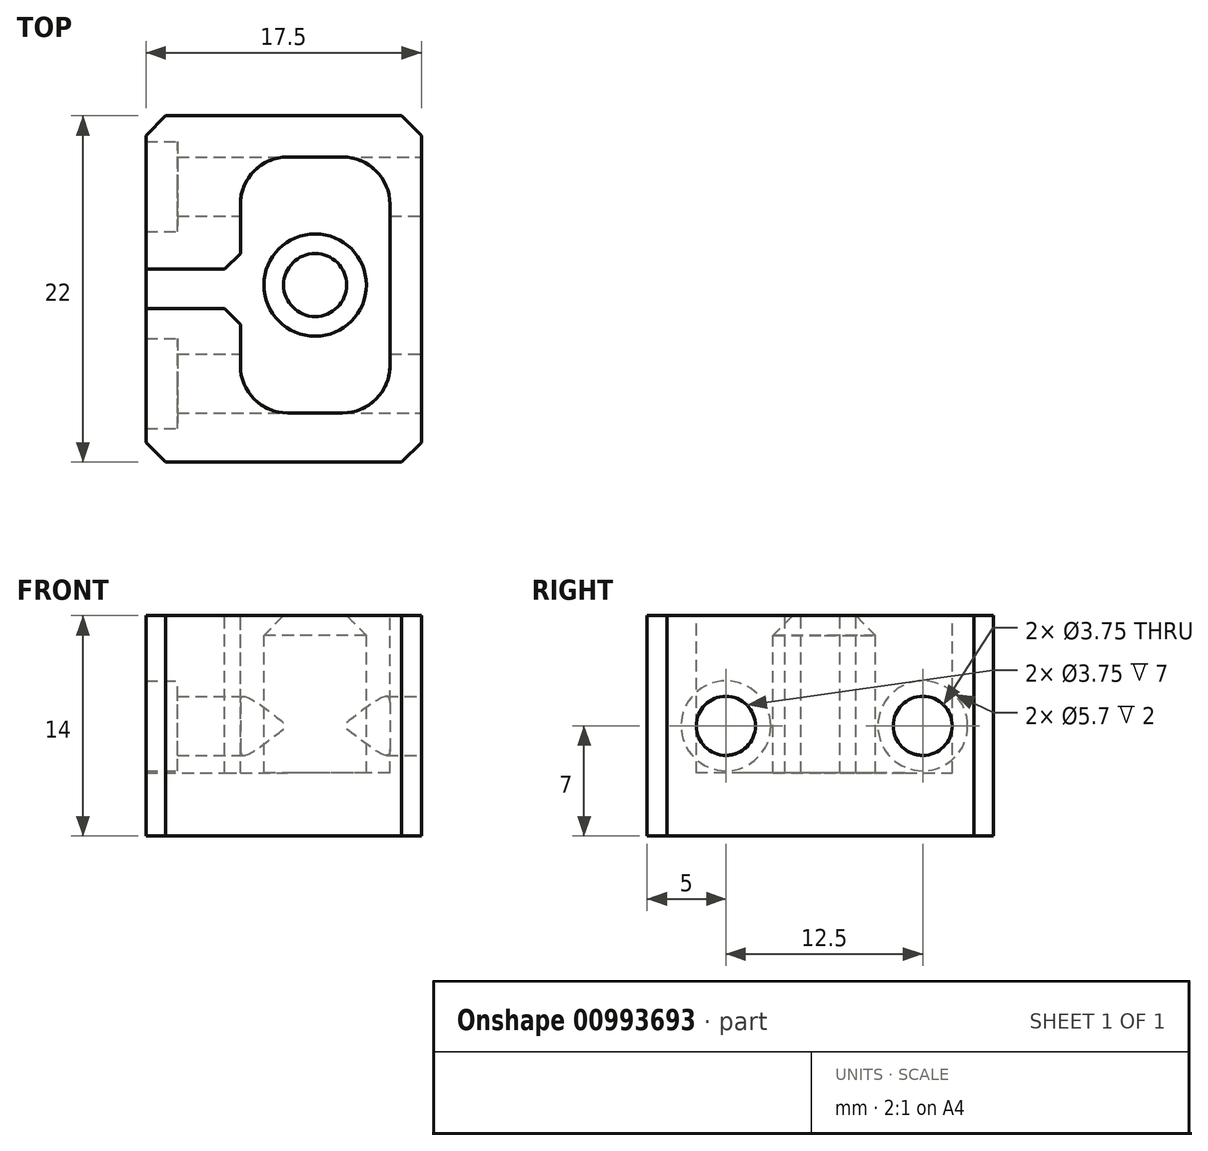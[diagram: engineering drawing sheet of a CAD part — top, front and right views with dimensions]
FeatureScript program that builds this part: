
annotation { "Feature Type Name" : "Feature", "Feature Type Description" : "" }
export const myFeature = defineFeature(function(context is Context, id is Id, definition is map)
    precondition{}
    {
        {
            var Q0;
            Q0=qCreatedBy(makeId("Top.planeOp"),FACE);
            var sketch = newSketch(context, id + "F0", { "sketchPlane" : qUnion([Q0])});
            skLineSegment(sketch, "E0.bottom", {"start": v(8.75, 11) * mm, "end": v(-8.75, 11) * mm});
            skLineSegment(sketch, "E0.top", {"start": v(8.75, -11) * mm, "end": v(-8.75, -11) * mm});
            skLineSegment(sketch, "E0.left", {"start": v(8.75, 11) * mm, "end": v(8.75, -11) * mm});
            skLineSegment(sketch, "E0.right", {"start": v(-8.75, 11) * mm, "end": v(-8.75, -11) * mm});
            skPoint(sketch, "E0.middle", {"position": v(0, 0) * mm});
            skLineSegment(sketch, "E1", {"start": v(-6.75, 8.37) * mm, "end": v(8.75, 8.38) * mm});
            skLineSegment(sketch, "E2", {"start": v(8.75, 4.63) * mm, "end": v(-6.75, 4.62) * mm});
            skLineSegment(sketch, "E3", {"start": v(8.75, -4.12) * mm, "end": v(-6.75, -4.13) * mm});
            skLineSegment(sketch, "E4", {"start": v(8.75, -7.87) * mm, "end": v(-6.75, -7.88) * mm});
            skLineSegment(sketch, "E5", {"start": v(-8.75, -1.25) * mm, "end": v(-2.75, -1.25) * mm});
            skLineSegment(sketch, "E6", {"start": v(-8.75, 1.25) * mm, "end": v(-2.75, 1.25) * mm});
            skLineSegment(sketch, "E7", {"start": v(-2.75, 1.25) * mm, "end": v(-2.75, 11) * mm});
            skLineSegment(sketch, "E8", {"start": v(-2.75, -1.25) * mm, "end": v(-2.75, -11) * mm});
            skCircle(sketch, "E9", {"center": v(2, 0.25) * mm, "radius": 4.75 * mm, "construction": true});
            skCircle(sketch, "E10", {"center": v(2, 0.25) * mm, "radius": 3.25 * mm});
            skLineSegment(sketch, "E11", {"start": v(-3.75, 1.25) * mm, "end": v(-2.75, 2.25) * mm});
            skLineSegment(sketch, "E12", {"start": v(-3.75, -1.25) * mm, "end": v(-2.75, -2.25) * mm});
            skLineSegment(sketch, "E13", {"start": v(6.75, 11) * mm, "end": v(6.75, -11) * mm});
            skLineSegment(sketch, "E14", {"start": v(-8.75, 6.5) * mm, "end": v(8.75, 6.5) * mm});
            skLineSegment(sketch, "E15", {"start": v(-8.75, -6) * mm, "end": v(8.75, -6) * mm});
            skLineSegment(sketch, "E16", {"start": v(-6.75, 8.37) * mm, "end": v(-6.75, 9.35) * mm});
            skLineSegment(sketch, "E17", {"start": v(-6.75, 9.35) * mm, "end": v(-8.75, 9.35) * mm});
            skLineSegment(sketch, "E18", {"start": v(-6.75, 4.62) * mm, "end": v(-6.75, 3.65) * mm});
            skLineSegment(sketch, "E19", {"start": v(-6.75, 3.65) * mm, "end": v(-8.75, 3.65) * mm});
            skLineSegment(sketch, "E20", {"start": v(-6.75, -4.13) * mm, "end": v(-6.75, -3.15) * mm});
            skLineSegment(sketch, "E21", {"start": v(-6.75, -3.15) * mm, "end": v(-8.75, -3.15) * mm});
            skLineSegment(sketch, "E22", {"start": v(-6.75, -7.88) * mm, "end": v(-6.75, -8.85) * mm});
            skLineSegment(sketch, "E23", {"start": v(-6.75, -8.85) * mm, "end": v(-8.75, -8.85) * mm});
            skSolve(sketch);
        }
        {
            var Q0;
            {var subQ3=sQuery(id+"F0.wireOp",EDGE,"E12");Q0=makeQuery(id+"F0.imprint","IMPRINT",FACE,{"disambiguationData":[TD([[makeQuery(id+"F0.imprint","IMPRINT",EDGE,{"derivedFrom":subQ3}),-1.0]])]});}
            var Q1;
            {var subQ0=sQuery(id+"F0.wireOp",EDGE,"E1");var subQ1=sQuery(id+"F0.wireOp",EDGE,"E0.right");var subQ2=makeQuery(id+"F0.imprint","INTERSECT",VERTEX,{"derivedFrom":[subQ1,subQ0]});Q1=makeQuery(id+"F0.imprint","IMPRINT",FACE,{"disambiguationData":[TD([[makeQuery(id+"F0.imprint","IMPRINT",EDGE,{"disambiguationData":[TD([[subQ2,-1.0]])],"derivedFrom":subQ1}),1.0]])]});}
            var Q2;
            {var subQ0=sQuery(id+"F0.wireOp",EDGE,"E1");var subQ1=sQuery(id+"F0.wireOp",EDGE,"E0.left");var subQ2=makeQuery(id+"F0.imprint","INTERSECT",VERTEX,{"derivedFrom":[subQ1,subQ0]});Q2=makeQuery(id+"F0.imprint","IMPRINT",FACE,{"disambiguationData":[TD([[makeQuery(id+"F0.imprint","IMPRINT",EDGE,{"disambiguationData":[TD([[subQ2,-1.0]])],"derivedFrom":subQ1}),-1.0]])]});}
            var Q3;
            {var subQ0=sQuery(id+"F0.wireOp",EDGE,"E3");var subQ1=sQuery(id+"F0.wireOp",EDGE,"E0.left");var subQ2=makeQuery(id+"F0.imprint","INTERSECT",VERTEX,{"derivedFrom":[subQ1,subQ0]});Q3=makeQuery(id+"F0.imprint","IMPRINT",FACE,{"disambiguationData":[TD([[makeQuery(id+"F0.imprint","IMPRINT",EDGE,{"disambiguationData":[TD([[subQ2,-1.0]])],"derivedFrom":subQ1}),-1.0]])]});}
            var Q4;
            {var subQ0=sQuery(id+"F0.wireOp",EDGE,"E0.right");var subQ1=sQuery(id+"F0.wireOp",EDGE,"E0.bottom");var subQ2=makeQuery(id+"F0.imprint","INTERSECT",VERTEX,{"derivedFrom":[subQ1,subQ0]});Q4=makeQuery(id+"F0.imprint","IMPRINT",FACE,{"disambiguationData":[TD([[makeQuery(id+"F0.imprint","IMPRINT",EDGE,{"disambiguationData":[TD([[subQ2,1.0]])],"derivedFrom":subQ1}),1.0]])]});}
            var Q5;
            {var subQ0=sQuery(id+"F0.wireOp",EDGE,"E0.left");var subQ1=sQuery(id+"F0.wireOp",EDGE,"E0.top");var subQ2=makeQuery(id+"F0.imprint","INTERSECT",VERTEX,{"derivedFrom":[subQ1,subQ0]});Q5=makeQuery(id+"F0.imprint","IMPRINT",FACE,{"disambiguationData":[TD([[makeQuery(id+"F0.imprint","IMPRINT",EDGE,{"disambiguationData":[TD([[subQ2,-1.0]])],"derivedFrom":subQ1}),-1.0]])]});}
            var Q6;
            {var subQ0=sQuery(id+"F0.wireOp",EDGE,"E3");var subQ1=sQuery(id+"F0.wireOp",EDGE,"E0.right");var subQ2=makeQuery(id+"F0.imprint","INTERSECT",VERTEX,{"derivedFrom":[subQ1,subQ0]});Q6=makeQuery(id+"F0.imprint","IMPRINT",FACE,{"disambiguationData":[TD([[makeQuery(id+"F0.imprint","IMPRINT",EDGE,{"disambiguationData":[TD([[subQ2,-1.0]])],"derivedFrom":subQ1}),1.0]])]});}
            var Q7;
            {var subQ0=sQuery(id+"F0.wireOp",EDGE,"E0.right");var subQ1=sQuery(id+"F0.wireOp",EDGE,"E0.top");var subQ2=makeQuery(id+"F0.imprint","INTERSECT",VERTEX,{"derivedFrom":[subQ1,subQ0]});Q7=makeQuery(id+"F0.imprint","IMPRINT",FACE,{"disambiguationData":[TD([[makeQuery(id+"F0.imprint","IMPRINT",EDGE,{"disambiguationData":[TD([[subQ2,1.0]])],"derivedFrom":subQ1}),-1.0]])]});}
            var Q8;
            {var subQ0=sQuery(id+"F0.wireOp",EDGE,"E0.left");var subQ1=sQuery(id+"F0.wireOp",EDGE,"E0.bottom");var subQ2=makeQuery(id+"F0.imprint","INTERSECT",VERTEX,{"derivedFrom":[subQ1,subQ0]});Q8=makeQuery(id+"F0.imprint","IMPRINT",FACE,{"disambiguationData":[TD([[makeQuery(id+"F0.imprint","IMPRINT",EDGE,{"disambiguationData":[TD([[subQ2,-1.0]])],"derivedFrom":subQ1}),1.0]])]});}
            var Q9;
            {var subQ3=sQuery(id+"F0.wireOp",EDGE,"E12");Q9=makeQuery(id+"F0.imprint","IMPRINT",FACE,{"disambiguationData":[TD([[makeQuery(id+"F0.imprint","IMPRINT",EDGE,{"derivedFrom":subQ3}),1.0]])]});}
            var Q10;
            {var subQ3=sQuery(id+"F0.wireOp",EDGE,"E11");Q10=makeQuery(id+"F0.imprint","IMPRINT",FACE,{"disambiguationData":[TD([[makeQuery(id+"F0.imprint","IMPRINT",EDGE,{"derivedFrom":subQ3}),-1.0]])]});}
            var Q11;
            {var subQ0=sQuery(id+"F0.wireOp",EDGE,"E11");Q11=makeQuery(id+"F0.imprint","IMPRINT",FACE,{"disambiguationData":[TD([[makeQuery(id+"F0.imprint","IMPRINT",EDGE,{"derivedFrom":subQ0}),1.0]])]});}
            var Q12;
            Q12=makeQuery(id+"F0.imprint","IMPRINT",FACE,{"disambiguationData":[TD([[makeQuery(id+"F0.imprint","IMPRINT",EDGE,{"derivedFrom":sQuery(id+"F0.wireOp",EDGE,"E10")}),-1.0]])]});
            var Q13;
            Q13=makeQuery(id+"F0.imprint","IMPRINT",FACE,{"disambiguationData":[TD([[makeQuery(id+"F0.imprint","IMPRINT",EDGE,{"derivedFrom":sQuery(id+"F0.wireOp",EDGE,"E10")}),1.0]])]});
            var Q14;
            {var subQ0=sQuery(id+"F0.wireOp",EDGE,"E7");var subQ1=sQuery(id+"F0.wireOp",EDGE,"E0.bottom");var subQ2=makeQuery(id+"F0.imprint","INTERSECT",VERTEX,{"derivedFrom":[subQ1,subQ0]});Q14=makeQuery(id+"F0.imprint","IMPRINT",FACE,{"disambiguationData":[TD([[makeQuery(id+"F0.imprint","IMPRINT",EDGE,{"disambiguationData":[TD([[subQ2,1.0]])],"derivedFrom":subQ1}),1.0]])]});}
            var Q15;
            {var subQ0=sQuery(id+"F0.wireOp",EDGE,"E7");var subQ1=sQuery(id+"F0.wireOp",EDGE,"E1");var subQ2=makeQuery(id+"F0.imprint","INTERSECT",VERTEX,{"derivedFrom":[subQ1,subQ0]});Q15=makeQuery(id+"F0.imprint","IMPRINT",FACE,{"disambiguationData":[TD([[makeQuery(id+"F0.imprint","IMPRINT",EDGE,{"disambiguationData":[TD([[subQ2,-1.0]])],"derivedFrom":subQ1}),-1.0]])]});}
            var Q16;
            {var subQ0=sQuery(id+"F0.wireOp",EDGE,"E2");var subQ1=sQuery(id+"F0.wireOp",EDGE,"E0.left");var subQ2=makeQuery(id+"F0.imprint","INTERSECT",VERTEX,{"derivedFrom":[subQ1,subQ0]});Q16=makeQuery(id+"F0.imprint","IMPRINT",FACE,{"disambiguationData":[TD([[makeQuery(id+"F0.imprint","IMPRINT",EDGE,{"disambiguationData":[TD([[subQ2,-1.0]])],"derivedFrom":subQ1}),-1.0]])]});}
            var Q17;
            {var subQ0=sQuery(id+"F0.wireOp",EDGE,"E13");var subQ1=sQuery(id+"F0.wireOp",EDGE,"E3");var subQ2=makeQuery(id+"F0.imprint","INTERSECT",VERTEX,{"derivedFrom":[subQ1,subQ0]});Q17=makeQuery(id+"F0.imprint","IMPRINT",FACE,{"disambiguationData":[TD([[makeQuery(id+"F0.imprint","IMPRINT",EDGE,{"disambiguationData":[TD([[subQ2,-1.0]])],"derivedFrom":subQ1}),1.0]])]});}
            var Q18;
            {var subQ0=sQuery(id+"F0.wireOp",EDGE,"E8");var subQ1=sQuery(id+"F0.wireOp",EDGE,"E0.top");var subQ2=makeQuery(id+"F0.imprint","INTERSECT",VERTEX,{"derivedFrom":[subQ1,subQ0]});Q18=makeQuery(id+"F0.imprint","IMPRINT",FACE,{"disambiguationData":[TD([[makeQuery(id+"F0.imprint","IMPRINT",EDGE,{"disambiguationData":[TD([[subQ2,1.0]])],"derivedFrom":subQ1}),-1.0]])]});}
            var Q19;
            {var subQ9=sQuery(id+"F0.wireOp",EDGE,"E16");Q19=makeQuery(id+"F0.imprint","IMPRINT",FACE,{"disambiguationData":[TD([[makeQuery(id+"F0.imprint","IMPRINT",EDGE,{"derivedFrom":subQ9}),1.0]])]});}
            var Q20;
            {var subQ6=sQuery(id+"F0.wireOp",EDGE,"E20");Q20=makeQuery(id+"F0.imprint","IMPRINT",FACE,{"disambiguationData":[TD([[makeQuery(id+"F0.imprint","IMPRINT",EDGE,{"derivedFrom":subQ6}),1.0]])]});}
            var Q21;
            {var subQ0=sQuery(id+"F0.wireOp",EDGE,"E13");var subQ1=sQuery(id+"F0.wireOp",EDGE,"E2");var subQ2=makeQuery(id+"F0.imprint","INTERSECT",VERTEX,{"derivedFrom":[subQ1,subQ0]});Q21=makeQuery(id+"F0.imprint","IMPRINT",FACE,{"disambiguationData":[TD([[makeQuery(id+"F0.imprint","IMPRINT",EDGE,{"disambiguationData":[TD([[subQ2,-1.0]])],"derivedFrom":subQ1}),-1.0]])]});}
            var Q22;
            {var subQ0=sQuery(id+"F0.wireOp",EDGE,"E2");var subQ1=sQuery(id+"F0.wireOp",EDGE,"E0.left");var subQ2=makeQuery(id+"F0.imprint","INTERSECT",VERTEX,{"derivedFrom":[subQ1,subQ0]});Q22=makeQuery(id+"F0.imprint","IMPRINT",FACE,{"disambiguationData":[TD([[makeQuery(id+"F0.imprint","IMPRINT",EDGE,{"disambiguationData":[TD([[subQ2,1.0]])],"derivedFrom":subQ1}),-1.0]])]});}
            var Q23;
            {var subQ0=sQuery(id+"F0.wireOp",EDGE,"E13");var subQ1=sQuery(id+"F0.wireOp",EDGE,"E4");var subQ2=makeQuery(id+"F0.imprint","INTERSECT",VERTEX,{"derivedFrom":[subQ1,subQ0]});Q23=makeQuery(id+"F0.imprint","IMPRINT",FACE,{"disambiguationData":[TD([[makeQuery(id+"F0.imprint","IMPRINT",EDGE,{"disambiguationData":[TD([[subQ2,-1.0]])],"derivedFrom":subQ1}),-1.0]])]});}
            var Q24;
            {var subQ0=sQuery(id+"F0.wireOp",EDGE,"E4");var subQ1=sQuery(id+"F0.wireOp",EDGE,"E0.left");var subQ2=makeQuery(id+"F0.imprint","INTERSECT",VERTEX,{"derivedFrom":[subQ1,subQ0]});Q24=makeQuery(id+"F0.imprint","IMPRINT",FACE,{"disambiguationData":[TD([[makeQuery(id+"F0.imprint","IMPRINT",EDGE,{"disambiguationData":[TD([[subQ2,1.0]])],"derivedFrom":subQ1}),-1.0]])]});}
            extrude(context, id + "F1", {"entities" : qUnion([Q0, Q1, Q2, Q3, Q4, Q5, Q6, Q7, Q8, Q9, Q10, Q11, Q12, Q13, Q14, Q15, Q16, Q17, Q18, Q19, Q20, Q21, Q22, Q23, Q24]), "oppositeDirection" : true, "depth" : (4 + 6 / 2) * mm, "offsetDistance" : 25 * mm});
        }
        {
            var Q0;
            Q0=makeQuery(id+"F0.imprint","IMPRINT",FACE,{"disambiguationData":[TD([[makeQuery(id+"F0.imprint","IMPRINT",EDGE,{"derivedFrom":sQuery(id+"F0.wireOp",EDGE,"E10")}),-1.0]])]});
            var Q1;
            {var subQ3=sQuery(id+"F0.wireOp",EDGE,"E12");Q1=makeQuery(id+"F0.imprint","IMPRINT",FACE,{"disambiguationData":[TD([[makeQuery(id+"F0.imprint","IMPRINT",EDGE,{"derivedFrom":subQ3}),1.0]])]});}
            var Q2;
            {var subQ3=sQuery(id+"F0.wireOp",EDGE,"E11");Q2=makeQuery(id+"F0.imprint","IMPRINT",FACE,{"disambiguationData":[TD([[makeQuery(id+"F0.imprint","IMPRINT",EDGE,{"derivedFrom":subQ3}),-1.0]])]});}
            var Q3;
            {var subQ0=sQuery(id+"F0.wireOp",EDGE,"E7");var subQ1=sQuery(id+"F0.wireOp",EDGE,"E1");var subQ2=makeQuery(id+"F0.imprint","INTERSECT",VERTEX,{"derivedFrom":[subQ1,subQ0]});Q3=makeQuery(id+"F0.imprint","IMPRINT",FACE,{"disambiguationData":[TD([[makeQuery(id+"F0.imprint","IMPRINT",EDGE,{"disambiguationData":[TD([[subQ2,-1.0]])],"derivedFrom":subQ1}),-1.0]])]});}
            var Q4;
            {var subQ0=sQuery(id+"F0.wireOp",EDGE,"E13");var subQ1=sQuery(id+"F0.wireOp",EDGE,"E3");var subQ2=makeQuery(id+"F0.imprint","INTERSECT",VERTEX,{"derivedFrom":[subQ1,subQ0]});Q4=makeQuery(id+"F0.imprint","IMPRINT",FACE,{"disambiguationData":[TD([[makeQuery(id+"F0.imprint","IMPRINT",EDGE,{"disambiguationData":[TD([[subQ2,-1.0]])],"derivedFrom":subQ1}),1.0]])]});}
            var Q5;
            {var subQ0=sQuery(id+"F0.wireOp",EDGE,"E13");var subQ1=sQuery(id+"F0.wireOp",EDGE,"E2");var subQ2=makeQuery(id+"F0.imprint","INTERSECT",VERTEX,{"derivedFrom":[subQ1,subQ0]});Q5=makeQuery(id+"F0.imprint","IMPRINT",FACE,{"disambiguationData":[TD([[makeQuery(id+"F0.imprint","IMPRINT",EDGE,{"disambiguationData":[TD([[subQ2,-1.0]])],"derivedFrom":subQ1}),-1.0]])]});}
            var Q6;
            {var subQ0=sQuery(id+"F0.wireOp",EDGE,"E13");var subQ1=sQuery(id+"F0.wireOp",EDGE,"E4");var subQ2=makeQuery(id+"F0.imprint","INTERSECT",VERTEX,{"derivedFrom":[subQ1,subQ0]});Q6=makeQuery(id+"F0.imprint","IMPRINT",FACE,{"disambiguationData":[TD([[makeQuery(id+"F0.imprint","IMPRINT",EDGE,{"disambiguationData":[TD([[subQ2,-1.0]])],"derivedFrom":subQ1}),-1.0]])]});}
            extrude(context, id + "F2", {"entities" : qUnion([Q0, Q1, Q2, Q3, Q4, Q5, Q6]), "operationType" : NewBodyOperationType.REMOVE, "oppositeDirection" : true, "depth" : (6 / 2) * mm, "offsetDistance" : 25 * mm});
        }
        {
            var Q0;
            {var subQ0=sQuery(id+"F0.wireOp",EDGE,"E11");Q0=makeQuery(id+"F0.imprint","IMPRINT",FACE,{"disambiguationData":[TD([[makeQuery(id+"F0.imprint","IMPRINT",EDGE,{"derivedFrom":subQ0}),1.0]])]});}
            var Q1;
            {var subQ0=sQuery(id+"F0.wireOp",EDGE,"E0.right");var subQ1=sQuery(id+"F0.wireOp",EDGE,"E0.bottom");var subQ2=makeQuery(id+"F0.imprint","INTERSECT",VERTEX,{"derivedFrom":[subQ1,subQ0]});Q1=makeQuery(id+"F0.imprint","IMPRINT",FACE,{"disambiguationData":[TD([[makeQuery(id+"F0.imprint","IMPRINT",EDGE,{"disambiguationData":[TD([[subQ2,1.0]])],"derivedFrom":subQ1}),1.0]])]});}
            var Q2;
            {var subQ0=sQuery(id+"F0.wireOp",EDGE,"E1");var subQ1=sQuery(id+"F0.wireOp",EDGE,"E0.right");var subQ2=makeQuery(id+"F0.imprint","INTERSECT",VERTEX,{"derivedFrom":[subQ1,subQ0]});Q2=makeQuery(id+"F0.imprint","IMPRINT",FACE,{"disambiguationData":[TD([[makeQuery(id+"F0.imprint","IMPRINT",EDGE,{"disambiguationData":[TD([[subQ2,-1.0]])],"derivedFrom":subQ1}),1.0]])]});}
            var Q3;
            {var subQ3=sQuery(id+"F0.wireOp",EDGE,"E12");Q3=makeQuery(id+"F0.imprint","IMPRINT",FACE,{"disambiguationData":[TD([[makeQuery(id+"F0.imprint","IMPRINT",EDGE,{"derivedFrom":subQ3}),-1.0]])]});}
            var Q4;
            {var subQ0=sQuery(id+"F0.wireOp",EDGE,"E3");var subQ1=sQuery(id+"F0.wireOp",EDGE,"E0.right");var subQ2=makeQuery(id+"F0.imprint","INTERSECT",VERTEX,{"derivedFrom":[subQ1,subQ0]});Q4=makeQuery(id+"F0.imprint","IMPRINT",FACE,{"disambiguationData":[TD([[makeQuery(id+"F0.imprint","IMPRINT",EDGE,{"disambiguationData":[TD([[subQ2,-1.0]])],"derivedFrom":subQ1}),1.0]])]});}
            var Q5;
            {var subQ0=sQuery(id+"F0.wireOp",EDGE,"E0.right");var subQ1=sQuery(id+"F0.wireOp",EDGE,"E0.top");var subQ2=makeQuery(id+"F0.imprint","INTERSECT",VERTEX,{"derivedFrom":[subQ1,subQ0]});Q5=makeQuery(id+"F0.imprint","IMPRINT",FACE,{"disambiguationData":[TD([[makeQuery(id+"F0.imprint","IMPRINT",EDGE,{"disambiguationData":[TD([[subQ2,1.0]])],"derivedFrom":subQ1}),-1.0]])]});}
            var Q6;
            {var subQ0=sQuery(id+"F0.wireOp",EDGE,"E0.left");var subQ1=sQuery(id+"F0.wireOp",EDGE,"E0.top");var subQ2=makeQuery(id+"F0.imprint","INTERSECT",VERTEX,{"derivedFrom":[subQ1,subQ0]});Q6=makeQuery(id+"F0.imprint","IMPRINT",FACE,{"disambiguationData":[TD([[makeQuery(id+"F0.imprint","IMPRINT",EDGE,{"disambiguationData":[TD([[subQ2,-1.0]])],"derivedFrom":subQ1}),-1.0]])]});}
            var Q7;
            {var subQ0=sQuery(id+"F0.wireOp",EDGE,"E0.left");var subQ1=sQuery(id+"F0.wireOp",EDGE,"E0.bottom");var subQ2=makeQuery(id+"F0.imprint","INTERSECT",VERTEX,{"derivedFrom":[subQ1,subQ0]});Q7=makeQuery(id+"F0.imprint","IMPRINT",FACE,{"disambiguationData":[TD([[makeQuery(id+"F0.imprint","IMPRINT",EDGE,{"disambiguationData":[TD([[subQ2,-1.0]])],"derivedFrom":subQ1}),1.0]])]});}
            var Q8;
            Q8=makeQuery(id+"F0.imprint","IMPRINT",FACE,{"disambiguationData":[TD([[makeQuery(id+"F0.imprint","IMPRINT",EDGE,{"derivedFrom":sQuery(id+"F0.wireOp",EDGE,"E10")}),1.0]])]});
            var Q9;
            {var subQ0=sQuery(id+"F0.wireOp",EDGE,"E7");var subQ1=sQuery(id+"F0.wireOp",EDGE,"E0.bottom");var subQ2=makeQuery(id+"F0.imprint","INTERSECT",VERTEX,{"derivedFrom":[subQ1,subQ0]});Q9=makeQuery(id+"F0.imprint","IMPRINT",FACE,{"disambiguationData":[TD([[makeQuery(id+"F0.imprint","IMPRINT",EDGE,{"disambiguationData":[TD([[subQ2,1.0]])],"derivedFrom":subQ1}),1.0]])]});}
            var Q10;
            {var subQ0=sQuery(id+"F0.wireOp",EDGE,"E1");var subQ1=sQuery(id+"F0.wireOp",EDGE,"E0.left");var subQ2=makeQuery(id+"F0.imprint","INTERSECT",VERTEX,{"derivedFrom":[subQ1,subQ0]});Q10=makeQuery(id+"F0.imprint","IMPRINT",FACE,{"disambiguationData":[TD([[makeQuery(id+"F0.imprint","IMPRINT",EDGE,{"disambiguationData":[TD([[subQ2,-1.0]])],"derivedFrom":subQ1}),-1.0]])]});}
            var Q11;
            {var subQ0=sQuery(id+"F0.wireOp",EDGE,"E2");var subQ1=sQuery(id+"F0.wireOp",EDGE,"E0.left");var subQ2=makeQuery(id+"F0.imprint","INTERSECT",VERTEX,{"derivedFrom":[subQ1,subQ0]});Q11=makeQuery(id+"F0.imprint","IMPRINT",FACE,{"disambiguationData":[TD([[makeQuery(id+"F0.imprint","IMPRINT",EDGE,{"disambiguationData":[TD([[subQ2,-1.0]])],"derivedFrom":subQ1}),-1.0]])]});}
            var Q12;
            {var subQ0=sQuery(id+"F0.wireOp",EDGE,"E3");var subQ1=sQuery(id+"F0.wireOp",EDGE,"E0.left");var subQ2=makeQuery(id+"F0.imprint","INTERSECT",VERTEX,{"derivedFrom":[subQ1,subQ0]});Q12=makeQuery(id+"F0.imprint","IMPRINT",FACE,{"disambiguationData":[TD([[makeQuery(id+"F0.imprint","IMPRINT",EDGE,{"disambiguationData":[TD([[subQ2,-1.0]])],"derivedFrom":subQ1}),-1.0]])]});}
            var Q13;
            {var subQ0=sQuery(id+"F0.wireOp",EDGE,"E8");var subQ1=sQuery(id+"F0.wireOp",EDGE,"E0.top");var subQ2=makeQuery(id+"F0.imprint","INTERSECT",VERTEX,{"derivedFrom":[subQ1,subQ0]});Q13=makeQuery(id+"F0.imprint","IMPRINT",FACE,{"disambiguationData":[TD([[makeQuery(id+"F0.imprint","IMPRINT",EDGE,{"disambiguationData":[TD([[subQ2,1.0]])],"derivedFrom":subQ1}),-1.0]])]});}
            var Q14;
            {var subQ9=sQuery(id+"F0.wireOp",EDGE,"E16");Q14=makeQuery(id+"F0.imprint","IMPRINT",FACE,{"disambiguationData":[TD([[makeQuery(id+"F0.imprint","IMPRINT",EDGE,{"derivedFrom":subQ9}),1.0]])]});}
            var Q15;
            {var subQ6=sQuery(id+"F0.wireOp",EDGE,"E20");Q15=makeQuery(id+"F0.imprint","IMPRINT",FACE,{"disambiguationData":[TD([[makeQuery(id+"F0.imprint","IMPRINT",EDGE,{"derivedFrom":subQ6}),1.0]])]});}
            var Q16;
            {var subQ0=sQuery(id+"F0.wireOp",EDGE,"E2");var subQ1=sQuery(id+"F0.wireOp",EDGE,"E0.left");var subQ2=makeQuery(id+"F0.imprint","INTERSECT",VERTEX,{"derivedFrom":[subQ1,subQ0]});Q16=makeQuery(id+"F0.imprint","IMPRINT",FACE,{"disambiguationData":[TD([[makeQuery(id+"F0.imprint","IMPRINT",EDGE,{"disambiguationData":[TD([[subQ2,1.0]])],"derivedFrom":subQ1}),-1.0]])]});}
            var Q17;
            {var subQ0=sQuery(id+"F0.wireOp",EDGE,"E4");var subQ1=sQuery(id+"F0.wireOp",EDGE,"E0.left");var subQ2=makeQuery(id+"F0.imprint","INTERSECT",VERTEX,{"derivedFrom":[subQ1,subQ0]});Q17=makeQuery(id+"F0.imprint","IMPRINT",FACE,{"disambiguationData":[TD([[makeQuery(id+"F0.imprint","IMPRINT",EDGE,{"disambiguationData":[TD([[subQ2,1.0]])],"derivedFrom":subQ1}),-1.0]])]});}
            extrude(context, id + "F3", {"entities" : qUnion([Q0, Q1, Q2, Q3, Q4, Q5, Q6, Q7, Q8, Q9, Q10, Q11, Q12, Q13, Q14, Q15, Q16, Q17]), "operationType" : NewBodyOperationType.ADD, "depth" : (4 + 6 / 2) * mm, "offsetDistance" : 25 * mm});
        }
        {
            var Q0;
            {var subQ0=sQuery(id+"F0.wireOp",EDGE,"E1");var subQ1=sQuery(id+"F0.wireOp",EDGE,"E13");Q0=makeQuery(id+"F5.boolean.opBoolean","SPLIT",EDGE,{"disambiguationData":[TD([makeQuery(id+"F3.opExtrude","CAP_FACE",FACE,{"disambiguationData":[OSD([sQuery(id+"F0.wireOp",EDGE,"E0.bottom"),sQuery(id+"F0.wireOp",EDGE,"E0.top"),sQuery(id+"F0.wireOp",EDGE,"E0.left"),sQuery(id+"F0.wireOp",EDGE,"E0.right"),subQ0,sQuery(id+"F0.wireOp",EDGE,"E4"),sQuery(id+"F0.wireOp",EDGE,"E5"),sQuery(id+"F0.wireOp",EDGE,"E6"),sQuery(id+"F0.wireOp",EDGE,"E7"),sQuery(id+"F0.wireOp",EDGE,"E8"),sQuery(id+"F0.wireOp",EDGE,"E11"),sQuery(id+"F0.wireOp",EDGE,"E12"),subQ1])],"isStart":false})])],"derivedFrom":makeQuery(id+"F3.boolean.opBoolean","MERGE",EDGE,{"derivedFrom":[makeQuery(id+"F2.boolean.opBoolean","COPY",EDGE,{"derivedFrom":makeQuery(id+"F2.opExtrude","SWEPT_EDGE",EDGE,{"disambiguationData":[OSD([subQ0,subQ1])]})}),makeQuery(id+"F3.opExtrude","SWEPT_EDGE",EDGE,{"disambiguationData":[OSD([subQ0,subQ1])]})]})});}
            var Q1;
            {var subQ0=sQuery(id+"F0.wireOp",EDGE,"E7");var subQ1=sQuery(id+"F0.wireOp",EDGE,"E1");Q1=makeQuery(id+"F3.boolean.opBoolean","MERGE",EDGE,{"derivedFrom":[makeQuery(id+"F2.boolean.opBoolean","COPY",EDGE,{"derivedFrom":makeQuery(id+"F2.opExtrude","SWEPT_EDGE",EDGE,{"disambiguationData":[OSD([subQ1,subQ0])]})}),makeQuery(id+"F3.opExtrude","SWEPT_EDGE",EDGE,{"disambiguationData":[OSD([subQ1,subQ0])]})]});}
            var Q2;
            {var subQ0=sQuery(id+"F0.wireOp",EDGE,"E13");var subQ1=sQuery(id+"F0.wireOp",EDGE,"E4");Q2=makeQuery(id+"F3.boolean.opBoolean","MERGE",EDGE,{"derivedFrom":[makeQuery(id+"F2.boolean.opBoolean","COPY",EDGE,{"derivedFrom":makeQuery(id+"F2.opExtrude","SWEPT_EDGE",EDGE,{"disambiguationData":[OSD([subQ1,subQ0])]})}),makeQuery(id+"F3.opExtrude","SWEPT_EDGE",EDGE,{"disambiguationData":[OSD([subQ1,subQ0])]})]});}
            var Q3;
            {var subQ0=sQuery(id+"F0.wireOp",EDGE,"E8");var subQ1=sQuery(id+"F0.wireOp",EDGE,"E4");Q3=makeQuery(id+"F3.boolean.opBoolean","MERGE",EDGE,{"derivedFrom":[makeQuery(id+"F2.boolean.opBoolean","COPY",EDGE,{"derivedFrom":makeQuery(id+"F2.opExtrude","SWEPT_EDGE",EDGE,{"disambiguationData":[OSD([subQ1,subQ0])]})}),makeQuery(id+"F3.opExtrude","SWEPT_EDGE",EDGE,{"disambiguationData":[OSD([subQ1,subQ0])]})]});}
            fillet(context, id + "F4", {"entities" : qUnion([Q0, Q1, Q2, Q3]), "radius" : 3 * mm, "tangentPropagation" : true, "allowEdgeOverflow" : false});
        }
        {
            var Q0;
            {var subQ0=sQuery(id+"F0.wireOp",EDGE,"E13");var subQ1=sQuery(id+"F0.wireOp",EDGE,"E2");var subQ2=makeQuery(id+"F0.imprint","INTERSECT",VERTEX,{"derivedFrom":[subQ1,subQ0]});Q0=makeQuery(id+"F0.imprint","IMPRINT",FACE,{"disambiguationData":[TD([[makeQuery(id+"F0.imprint","IMPRINT",EDGE,{"disambiguationData":[TD([[subQ2,-1.0]])],"derivedFrom":subQ1}),-1.0]])]});}
            var Q1;
            {var subQ6=sQuery(id+"F0.wireOp",EDGE,"E18");Q1=makeQuery(id+"F0.imprint","IMPRINT",FACE,{"disambiguationData":[TD([[makeQuery(id+"F0.imprint","IMPRINT",EDGE,{"derivedFrom":subQ6}),-1.0]])]});}
            var Q2;
            {var subQ0=sQuery(id+"F0.wireOp",EDGE,"E2");var subQ1=sQuery(id+"F0.wireOp",EDGE,"E0.left");var subQ2=makeQuery(id+"F0.imprint","INTERSECT",VERTEX,{"derivedFrom":[subQ1,subQ0]});Q2=makeQuery(id+"F0.imprint","IMPRINT",FACE,{"disambiguationData":[TD([[makeQuery(id+"F0.imprint","IMPRINT",EDGE,{"disambiguationData":[TD([[subQ2,1.0]])],"derivedFrom":subQ1}),-1.0]])]});}
            var Q3;
            Q3=sQuery(id+"F0.wireOp",EDGE,"E14");
            revolve(context, id + "F5", {"operationType" : NewBodyOperationType.REMOVE, "surfaceOperationType" : NewSurfaceOperationType.NEW, "entities" : qUnion([Q0, Q1, Q2]), "axis" : qUnion([Q3]), "revolveType" : RevolveType.FULL, "oppositeDirection" : true});
        }
        {
            var Q0;
            {var subQ0=sQuery(id+"F0.wireOp",EDGE,"E13");var subQ1=sQuery(id+"F0.wireOp",EDGE,"E4");var subQ2=makeQuery(id+"F0.imprint","INTERSECT",VERTEX,{"derivedFrom":[subQ1,subQ0]});Q0=makeQuery(id+"F0.imprint","IMPRINT",FACE,{"disambiguationData":[TD([[makeQuery(id+"F0.imprint","IMPRINT",EDGE,{"disambiguationData":[TD([[subQ2,-1.0]])],"derivedFrom":subQ1}),-1.0]])]});}
            var Q1;
            {var subQ0=sQuery(id+"F0.wireOp",EDGE,"E4");var subQ1=sQuery(id+"F0.wireOp",EDGE,"E0.left");var subQ2=makeQuery(id+"F0.imprint","INTERSECT",VERTEX,{"derivedFrom":[subQ1,subQ0]});Q1=makeQuery(id+"F0.imprint","IMPRINT",FACE,{"disambiguationData":[TD([[makeQuery(id+"F0.imprint","IMPRINT",EDGE,{"disambiguationData":[TD([[subQ2,1.0]])],"derivedFrom":subQ1}),-1.0]])]});}
            var Q2;
            {var subQ7=sQuery(id+"F0.wireOp",EDGE,"E22");Q2=makeQuery(id+"F0.imprint","IMPRINT",FACE,{"disambiguationData":[TD([[makeQuery(id+"F0.imprint","IMPRINT",EDGE,{"derivedFrom":subQ7}),-1.0]])]});}
            var Q3;
            Q3=sQuery(id+"F0.wireOp",EDGE,"E15");
            revolve(context, id + "F6", {"operationType" : NewBodyOperationType.REMOVE, "surfaceOperationType" : NewSurfaceOperationType.NEW, "entities" : qUnion([Q0, Q1, Q2]), "axis" : qUnion([Q3]), "revolveType" : RevolveType.FULL, "oppositeDirection" : true});
        }
        {
            var Q0;
            {var subQ0=sQuery(id+"F0.wireOp",EDGE,"E0.right");var subQ1=sQuery(id+"F0.wireOp",EDGE,"E0.bottom");Q0=makeQuery(id+"F3.boolean.opBoolean","MERGE",EDGE,{"derivedFrom":[makeQuery(id+"F1.opExtrude","SWEPT_EDGE",EDGE,{"disambiguationData":[OSD([subQ1,subQ0])]}),makeQuery(id+"F3.opExtrude","SWEPT_EDGE",EDGE,{"disambiguationData":[OSD([subQ1,subQ0])]})]});}
            var Q1;
            {var subQ0=sQuery(id+"F0.wireOp",EDGE,"E0.right");var subQ1=sQuery(id+"F0.wireOp",EDGE,"E0.top");Q1=makeQuery(id+"F3.boolean.opBoolean","MERGE",EDGE,{"derivedFrom":[makeQuery(id+"F1.opExtrude","SWEPT_EDGE",EDGE,{"disambiguationData":[OSD([subQ1,subQ0])]}),makeQuery(id+"F3.opExtrude","SWEPT_EDGE",EDGE,{"disambiguationData":[OSD([subQ1,subQ0])]})]});}
            var Q2;
            {var subQ0=sQuery(id+"F0.wireOp",EDGE,"E0.left");var subQ1=sQuery(id+"F0.wireOp",EDGE,"E0.top");Q2=makeQuery(id+"F3.boolean.opBoolean","MERGE",EDGE,{"derivedFrom":[makeQuery(id+"F1.opExtrude","SWEPT_EDGE",EDGE,{"disambiguationData":[OSD([subQ1,subQ0])]}),makeQuery(id+"F3.opExtrude","SWEPT_EDGE",EDGE,{"disambiguationData":[OSD([subQ1,subQ0])]})]});}
            var Q3;
            {var subQ0=sQuery(id+"F0.wireOp",EDGE,"E0.left");var subQ1=sQuery(id+"F0.wireOp",EDGE,"E0.bottom");Q3=makeQuery(id+"F3.boolean.opBoolean","MERGE",EDGE,{"derivedFrom":[makeQuery(id+"F1.opExtrude","SWEPT_EDGE",EDGE,{"disambiguationData":[OSD([subQ1,subQ0])]}),makeQuery(id+"F3.opExtrude","SWEPT_EDGE",EDGE,{"disambiguationData":[OSD([subQ1,subQ0])]})]});}
            var Q4;
            Q4=makeQuery(id+"F3.opExtrude","CAP_EDGE",EDGE,{"disambiguationData":[OSD([sQuery(id+"F0.wireOp",EDGE,"E10")])],"isStart":false});
            chamfer(context, id + "F7", {"entities" : qUnion([Q0, Q1, Q2, Q3, Q4]), "width" : 1.25 * mm, "tangentPropagation" : true});
        }
    });
